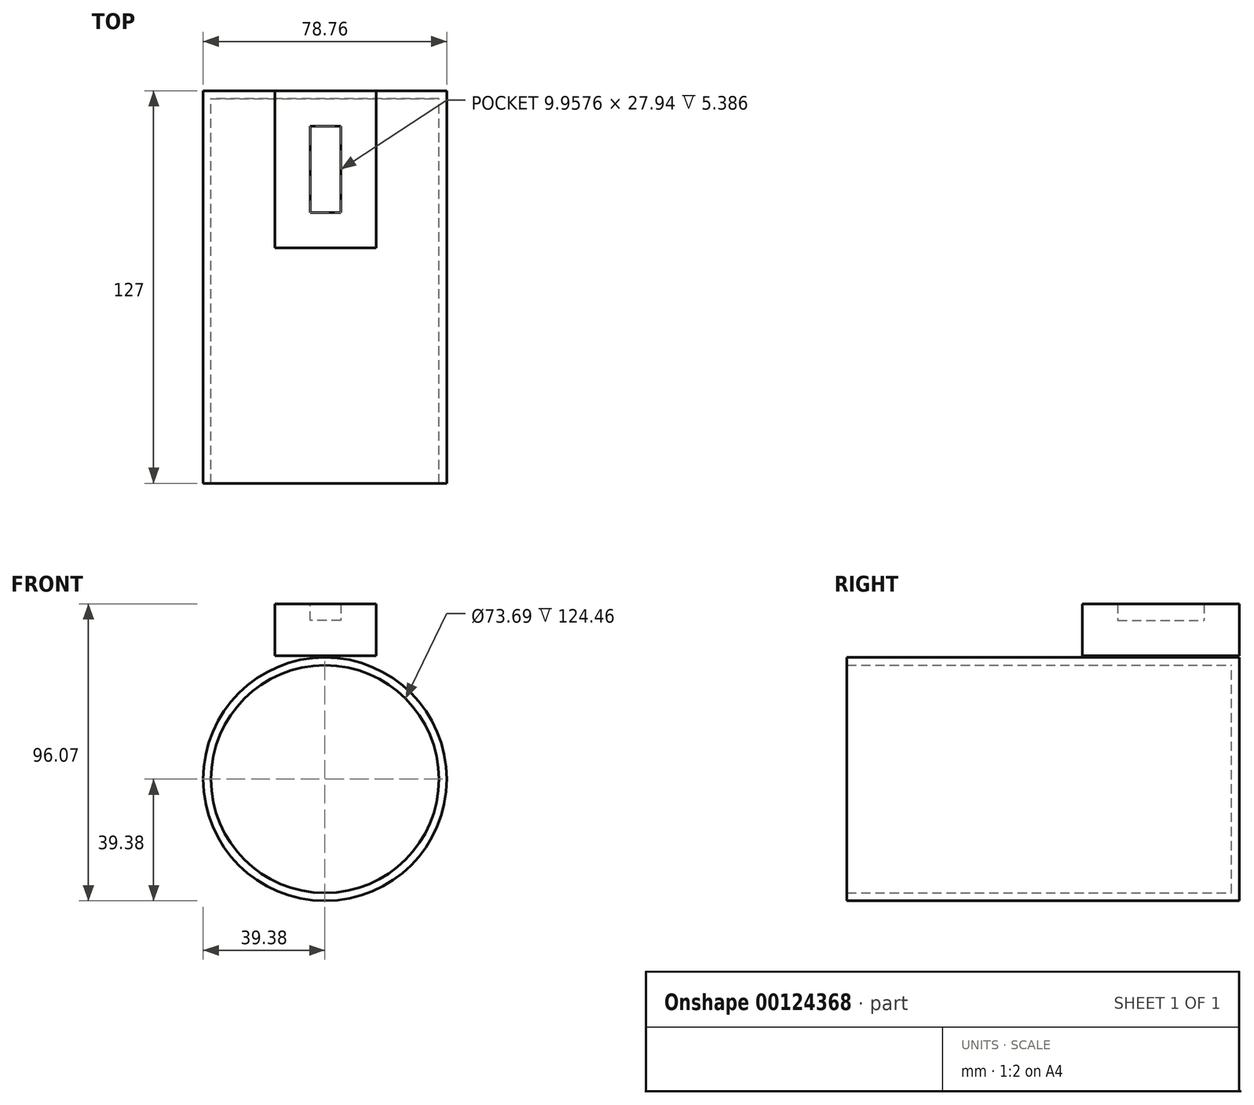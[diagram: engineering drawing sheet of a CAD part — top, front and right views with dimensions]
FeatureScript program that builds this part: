
annotation { "Feature Type Name" : "Feature", "Feature Type Description" : "" }
export const myFeature = defineFeature(function(context is Context, id is Id, definition is map)
    precondition{}
    {
        {
            var Q0;
            Q0=qCreatedBy(makeId("Front.planeOp"),FACE);
            var sketch = newSketch(context, id + "F0", { "sketchPlane" : qUnion([Q0])});
            skCircle(sketch, "E0", {"center": v(0, 0) * mm, "radius": 39.38 * mm});
            skSolve(sketch);
        }
        {
            var Q0;
            Q0 = qSketchRegion(id + "F0", true);
            var Q1;
            Q1=makeQuery(id+"F0.imprint","IMPRINT",FACE,{"disambiguationData":[TD([[makeQuery(id+"F0.imprint","IMPRINT",EDGE,{"derivedFrom":sQuery(id+"F0.wireOp",EDGE,"E0")}),1.0]])]});
            extrude(context, id + "F1", {"entities" : qUnion([Q0, Q1]), "depth" : 127 * mm});
        }
        {
            var Q0;
            Q0=makeQuery(id+"F1.opExtrude","CAP_FACE",FACE,{"disambiguationData":[OSD([sQuery(id+"F0.wireOp",EDGE,"E0")])],"isStart":false});
            shell(context, id + "F2", {"entities" : qUnion([Q0]), "thickness" : 2.54 * mm});
        }
        {
            var Q0;
            Q0=qCreatedBy(makeId("Front.planeOp"),FACE);
            var sketch = newSketch(context, id + "F3", { "sketchPlane" : qUnion([Q0])});
            skLineSegment(sketch, "E1", {"start": v(0, 39.87) * mm, "end": v(-16.24, 39.87) * mm});
            skLineSegment(sketch, "E2", {"start": v(-16.24, 39.87) * mm, "end": v(-16.24, 56.69) * mm});
            skLineSegment(sketch, "E3", {"start": v(-16.24, 56.69) * mm, "end": v(16.58, 56.69) * mm});
            skLineSegment(sketch, "E4", {"start": v(16.58, 56.69) * mm, "end": v(16.58, 39.87) * mm});
            skLineSegment(sketch, "E5", {"start": v(16.58, 39.87) * mm, "end": v(0, 39.87) * mm});
            skSolve(sketch);
        }
        {
            var Q0;
            Q0=makeQuery(id+"F3.imprint","IMPRINT",FACE,{"disambiguationData":[TD([[makeQuery(id+"F3.imprint","IMPRINT",EDGE,{"derivedFrom":sQuery(id+"F3.wireOp",EDGE,"E1")}),-1.0]])]});
            extrude(context, id + "F4", {"entities" : qUnion([Q0]), "depth" : 50.8 * mm});
        }
        {
            var Q0;
            Q0=makeQuery(id+"F4.opExtrude","SWEPT_FACE",FACE,{"disambiguationData":[OSD([sQuery(id+"F3.wireOp",EDGE,"E3")])]});
            shell(context, id + "F5", {"entities" : qUnion([Q0]), "thickness" : 11.43 * mm});
        }
    });
